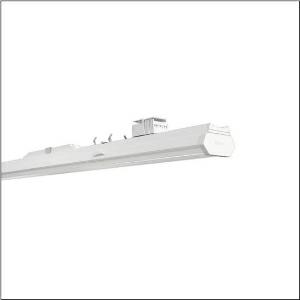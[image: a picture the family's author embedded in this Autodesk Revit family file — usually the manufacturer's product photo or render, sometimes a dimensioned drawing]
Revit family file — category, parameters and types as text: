
# Revit family: licross_r__11_protected_ho_51td1bcn4d5m_12de
name_source: partatom
category: Lighting Fixtures
units: mm (PartAtom-declared; Revit-internal decimal feet)

## family parameters
Cut with Voids When Loaded = No
Host = Face
Light Source = No
Part Type = Normal
Room Calculation Point = No
Round Connector Dimension = Use Diameter
Shared = No

## types (1)
- --- (1 x LED, 13520 lm, 77.6 W, 4000K)
    Apparent Load = 78 VA
    CIE Flux Codes = 54 82 95 97 100
    Color Rendering = 80
    Color Temperature = 4000K
    Default Elevation = 1800 mm
    Description = Licross® 11 Protected HO, luminaire insert, of sheet steel, galvanised, coil coated, white, length: 1.500mm, width: 90mm, height: 101mm, LED rated luminous flux: 13.520lm, light colour: 840, control gear: ON/OFF Multilumen, CLOi, with plug, 3-pole, with phase selection, mains connection: 220..240V, AC, 50/60Hz, start of lifetime: 78W, end of service life: 87W, internal wiring halogen-free, primary optical cover: cover, of PMMA, light emission: direct distribution, primary light characteristic: symmetric, protection rating (complete): IP54, insulation class (complete): insulation class I (protective earthing), certification: CE, ENEC, VDE, UKCA, protection symbol: D if used in an environment with non-conductive dust loads with corresponding accessories, impact resistance: IK06, permissible ambient temperature for indoor applications: -35..+35°C, corresponds to IFS (International Featured Standards) requirements for safety and quality in the food industry, reducing of maximum allowable ambient temperature of 5°C with ceiling mounting, LABS conformity tested according to VDMA 24364:2018-05, packaging unit: 1 piece
    Height = 92 mm
    Lamp = 1 x LED
    Lamp Light Flux = 13520 lm
    Lamp Power = 77.6 W
    Lamp count = 1
    Length = 1500 mm
    Luminous efficacy = 174 lm/W
    Manufacturer = Siteco
    ModVariant = No
    Model = 51TD1BCN4D5M
    Mounting Place = Ceiling
    Mounting Type = Pendant
    Number of Poles = 1
    OnlyDefault = Yes
    Power Factor = 1
    Product Name = Licross® 11 Protected HO
    Product group = luminaire insert | ceiling pendant
    ProductGroupID = 902
    Protection Class = Protection class I
    Protection Degree = IP 54
    RLX_Detail_Level = 1
    RLX_Emergency_Light_Flux = 0 lm
    RLX_Emergency_Type = 0
    RLX_Emergency_Type_DB = No
    RlxData = <blob elided: 22093 chars, md5=164dd361>
    Socket = socket
    Standby Power = 0 W
    System Light Flux = 13520 lm
    System Power = 78 W
    Type Comments = factory setting: luminous flux: 100 % | (A | C | E) | 181 mA
    Type Image = l_1256145.jpg
    URL = http://relux.com
    VarID = @adj_107555
    Voltage = 0 V
    Weight = 0.00 kg
    Width = 88 mm

## geometry (parser evidence)
native form markers: Blend x4, Sweep x11
no freeform markers — native parametric forms only
